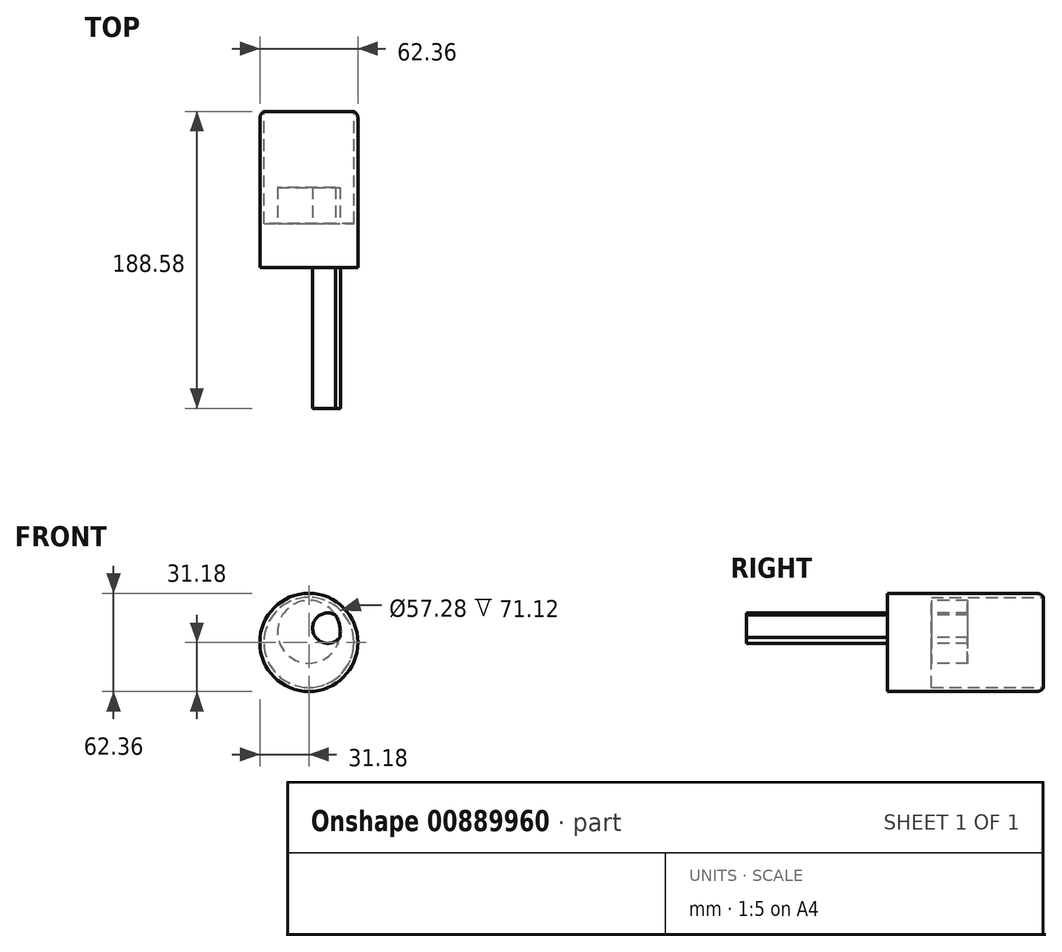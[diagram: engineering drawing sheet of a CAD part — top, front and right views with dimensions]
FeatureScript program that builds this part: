
annotation { "Feature Type Name" : "Feature", "Feature Type Description" : "" }
export const myFeature = defineFeature(function(context is Context, id is Id, definition is map)
    precondition{}
    {
        {
            var Q0;
            Q0=qCreatedBy(makeId("Front.planeOp"),FACE);
            var sketch = newSketch(context, id + "F0", { "sketchPlane" : qUnion([Q0])});
            skCircle(sketch, "E0", {"center": v(0, 0) * mm, "radius": 31.18 * mm});
            skSolve(sketch);
        }
        {
            var Q0;
            Q0=makeQuery(id+"F0.imprint","IMPRINT",FACE,{"disambiguationData":[TD([[makeQuery(id+"F0.imprint","IMPRINT",EDGE,{"derivedFrom":sQuery(id+"F0.wireOp",EDGE,"E0")}),1.0]])]});
            extrude(context, id + "F1", {"entities" : qUnion([Q0]), "depth" : 73.66 * mm, "offsetDistance" : 25.4 * mm});
        }
        {
            var Q0;
            Q0=makeQuery(id+"F1.opExtrude","CAP_FACE",FACE,{"disambiguationData":[OSD([sQuery(id+"F0.wireOp",EDGE,"E0")])],"isStart":true});
            shell(context, id + "F2", {"entities" : qUnion([Q0]), "thickness" : 2.54 * mm});
        }
        {
            var Q0;
            Q0=makeQuery(id+"F1.opExtrude","CAP_EDGE",EDGE,{"disambiguationData":[OSD([sQuery(id+"F0.wireOp",EDGE,"E0")])],"isStart":true});
            fillet(context, id + "F3", {"entities" : qUnion([Q0]), "radius" : 5.08 * mm, "tangentPropagation" : true, "allowEdgeOverflow" : false});
        }
        {
            var Q0;
            Q0=makeQuery(id+"F1.opExtrude","CAP_FACE",FACE,{"disambiguationData":[OSD([sQuery(id+"F0.wireOp",EDGE,"E0")])],"isStart":false});
            var sketch = newSketch(context, id + "F4", { "sketchPlane" : qUnion([Q0])});
            skCircle(sketch, "E1", {"center": v(0, 6.77) * mm, "radius": 19.95 * mm});
            skCircle(sketch, "E2", {"center": v(11.99, 9.1) * mm, "radius": 9.64 * mm});
            skSolve(sketch);
        }
        {
            var Q0;
            {var subQ0=sQuery(id+"F4.wireOp",EDGE,"E2");var subQ1=sQuery(id+"F4.wireOp",EDGE,"E1");var subQ2=makeQuery(id+"F4.imprint","INTERSECT",VERTEX,{"disambiguationData":[OD(0.0)],"derivedFrom":[subQ1,subQ0]});Q0=makeQuery(id+"F4.imprint","IMPRINT",FACE,{"disambiguationData":[TD([[makeQuery(id+"F4.imprint","IMPRINT",EDGE,{"disambiguationData":[TD([[subQ2,1.0]])],"derivedFrom":subQ1}),1.0]])]});}
            var sketch = newSketch(context, id + "F5", { "sketchPlane" : qUnion([Q0])});
            skSolve(sketch);
        }
        {
            var Q0;
            {var subQ0=sQuery(id+"F4.wireOp",EDGE,"E2");var subQ1=sQuery(id+"F4.wireOp",EDGE,"E1");var subQ2=makeQuery(id+"F4.imprint","INTERSECT",VERTEX,{"disambiguationData":[OD(0.0)],"derivedFrom":[subQ1,subQ0]});Q0=makeQuery(id+"F4.imprint","IMPRINT",FACE,{"disambiguationData":[TD([[makeQuery(id+"F4.imprint","IMPRINT",EDGE,{"disambiguationData":[TD([[subQ2,1.0]])],"derivedFrom":subQ1}),1.0]])]});}
            var sketch = newSketch(context, id + "F6", { "sketchPlane" : qUnion([Q0])});
            skSolve(sketch);
        }
        {
            var Q0;
            {var subQ0=sQuery(id+"F4.wireOp",EDGE,"E2");var subQ1=sQuery(id+"F4.wireOp",EDGE,"E1");var subQ2=makeQuery(id+"F4.imprint","INTERSECT",VERTEX,{"disambiguationData":[OD(0.0)],"derivedFrom":[subQ1,subQ0]});Q0=makeQuery(id+"F4.imprint","IMPRINT",FACE,{"disambiguationData":[TD([[makeQuery(id+"F4.imprint","IMPRINT",EDGE,{"disambiguationData":[TD([[subQ2,-1.0]])],"derivedFrom":subQ1}),1.0]])]});}
            extrude(context, id + "F7", {"entities" : qUnion([Q0]), "operationType" : NewBodyOperationType.ADD, "endBound" : BoundingType.THROUGH_ALL, "depth" : 50.8 * mm, "offsetDistance" : 25.4 * mm});
        }
        {
            var Q0;
            {var subQ0=sQuery(id+"F4.wireOp",EDGE,"E2");var subQ1=sQuery(id+"F4.wireOp",EDGE,"E1");var subQ2=makeQuery(id+"F4.imprint","INTERSECT",VERTEX,{"disambiguationData":[OD(0.0)],"derivedFrom":[subQ1,subQ0]});Q0=makeQuery(id+"F6.imprint","IMPRINT",FACE,{"disambiguationData":[TD([[makeQuery(id+"F6.imprint","IMPRINT",EDGE,{"derivedFrom":makeQuery(id+"F4.imprint","IMPRINT",EDGE,{"disambiguationData":[TD([[subQ2,1.0]])],"derivedFrom":subQ1})}),1.0]])]});}
            extrude(context, id + "F8", {"entities" : qUnion([Q0]), "operationType" : NewBodyOperationType.ADD, "oppositeDirection" : true, "depth" : 25.4 * mm, "offsetDistance" : 25.4 * mm});
        }
        {
            var Q0;
            {var subQ0=sQuery(id+"F4.wireOp",EDGE,"E2");var subQ1=sQuery(id+"F4.wireOp",EDGE,"E1");var subQ2=makeQuery(id+"F4.imprint","INTERSECT",VERTEX,{"disambiguationData":[OD(0.0)],"derivedFrom":[subQ1,subQ0]});Q0=makeQuery(id+"F5.imprint","IMPRINT",FACE,{"disambiguationData":[TD([[makeQuery(id+"F5.imprint","IMPRINT",EDGE,{"derivedFrom":makeQuery(id+"F4.imprint","IMPRINT",EDGE,{"disambiguationData":[TD([[subQ2,1.0]])],"derivedFrom":subQ1})}),1.0]])]});}
            var Q1;
            Q1=makeQuery(id+"F1.opExtrude","CAP_FACE",FACE,{"disambiguationData":[OSD([sQuery(id+"F0.wireOp",EDGE,"E0")])],"isStart":false});
            extrude(context, id + "F9", {"entities" : qUnion([Q0, Q1]), "operationType" : NewBodyOperationType.ADD, "depth" : 25.4 * mm, "offsetDistance" : 25.4 * mm});
        }
    });
